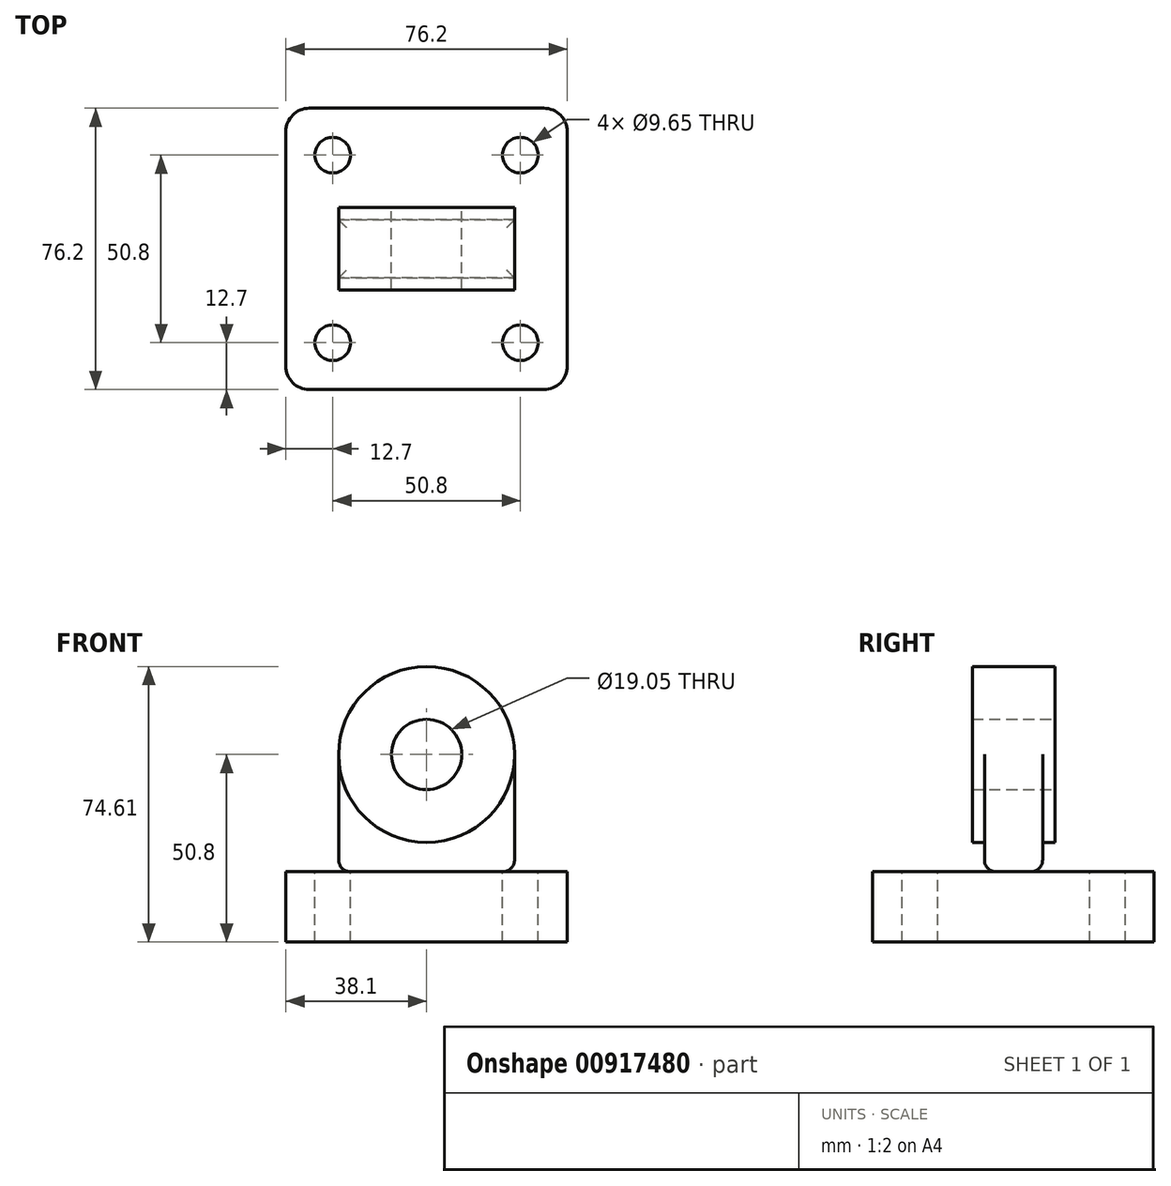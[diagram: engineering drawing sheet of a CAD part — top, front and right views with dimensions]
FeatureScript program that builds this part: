
annotation { "Feature Type Name" : "Feature", "Feature Type Description" : "" }
export const myFeature = defineFeature(function(context is Context, id is Id, definition is map)
    precondition{}
    {
        {
            var Q0;
            Q0=qCreatedBy(makeId("Top.planeOp"),FACE);
            var sketch = newSketch(context, id + "F0", { "sketchPlane" : qUnion([Q0])});
            skLineSegment(sketch, "E0.bottom", {"start": v(0, 0) * mm, "end": v(76.2, 0) * mm});
            skLineSegment(sketch, "E0.top", {"start": v(0, 76.2) * mm, "end": v(76.2, 76.2) * mm});
            skLineSegment(sketch, "E0.left", {"start": v(0, 0) * mm, "end": v(0, 76.2) * mm});
            skLineSegment(sketch, "E0.right", {"start": v(76.2, 0) * mm, "end": v(76.2, 76.2) * mm});
            skSolve(sketch);
        }
        {
            var Q0;
            Q0=makeQuery(id+"F0.imprint","IMPRINT",FACE,{"disambiguationData":[TD([[makeQuery(id+"F0.imprint","IMPRINT",EDGE,{"derivedFrom":sQuery(id+"F0.wireOp",EDGE,"E0.bottom")}),1.0]])]});
            extrude(context, id + "F1", {"entities" : qUnion([Q0]), "depth" : 19.05 * mm, "offsetDistance" : 25.4 * mm});
        }
        {
            var Q0;
            Q0=makeQuery(id+"F1.opExtrude","CAP_FACE",FACE,{"disambiguationData":[OSD([sQuery(id+"F0.wireOp",EDGE,"E0.bottom"),sQuery(id+"F0.wireOp",EDGE,"E0.top"),sQuery(id+"F0.wireOp",EDGE,"E0.left"),sQuery(id+"F0.wireOp",EDGE,"E0.right")])],"isStart":false});
            var sketch = newSketch(context, id + "F2", { "sketchPlane" : qUnion([Q0])});
            skPoint(sketch, "E1", {"position": v(12.7, 12.7) * mm});
            skPoint(sketch, "E2", {"position": v(63.5, 12.7) * mm});
            skPoint(sketch, "E3", {"position": v(12.7, 63.5) * mm});
            skPoint(sketch, "E4", {"position": v(63.5, 63.5) * mm});
            skSolve(sketch);
        }
        {
            var Q0;
            Q0=sQuery(id+"F2.wireOp",VERTEX,"E3");
            var Q1;
            Q1=sQuery(id+"F2.wireOp",VERTEX,"E4");
            var Q2;
            Q2=sQuery(id+"F2.wireOp",VERTEX,"E2");
            var Q3;
            Q3=sQuery(id+"F2.wireOp",VERTEX,"E1");
            var Q4;
            Q4=makeQuery(id+"F1.opExtrude","SWEPT_BODY",BODY,{"disambiguationData":[OSD([sQuery(id+"F0.wireOp",EDGE,"E0.bottom"),sQuery(id+"F0.wireOp",EDGE,"E0.top"),sQuery(id+"F0.wireOp",EDGE,"E0.left"),sQuery(id+"F0.wireOp",EDGE,"E0.right")])]});
            hole(context, id + "F3", {"style" : HoleStyle.SIMPLE, "endStyle" : HoleEndStyle.THROUGH, "holeDiameter" : 9.65 * mm, "majorDiameter" : 6.35 * mm, "isTappedThrough" : true, "tappedDepth" : 12.7 * mm, "tapClearance" : 3, "locations" : qUnion([Q0, Q1, Q2, Q3]), "scope" : qUnion([Q4])});
        }
        {
            var Q0;
            Q0=makeQuery(id+"F1.opExtrude","CAP_FACE",FACE,{"disambiguationData":[OSD([sQuery(id+"F0.wireOp",EDGE,"E0.bottom"),sQuery(id+"F0.wireOp",EDGE,"E0.top"),sQuery(id+"F0.wireOp",EDGE,"E0.left"),sQuery(id+"F0.wireOp",EDGE,"E0.right")])],"isStart":false});
            var sketch = newSketch(context, id + "F4", { "sketchPlane" : qUnion([Q0])});
            skLineSegment(sketch, "E5.bottom", {"start": v(61.91, 45.97) * mm, "end": v(14.29, 45.97) * mm});
            skLineSegment(sketch, "E5.top", {"start": v(61.91, 30.23) * mm, "end": v(14.29, 30.23) * mm});
            skLineSegment(sketch, "E5.left", {"start": v(61.91, 45.97) * mm, "end": v(61.91, 30.23) * mm});
            skLineSegment(sketch, "E5.right", {"start": v(14.29, 45.97) * mm, "end": v(14.29, 30.23) * mm});
            skPoint(sketch, "E5.middle", {"position": v(38.1, 38.1) * mm});
            skSolve(sketch);
        }
        {
            var Q0;
            Q0=makeQuery(id+"F4.imprint","IMPRINT",FACE,{"disambiguationData":[TD([[makeQuery(id+"F4.imprint","IMPRINT",EDGE,{"derivedFrom":sQuery(id+"F4.wireOp",EDGE,"E5.bottom")}),1.0]])]});
            extrude(context, id + "F5", {"entities" : qUnion([Q0]), "depth" : 55.56 * mm, "offsetDistance" : 25.4 * mm});
        }
        {
            var Q0;
            Q0=makeQuery(id+"F5.opExtrude","SWEPT_FACE",FACE,{"disambiguationData":[OSD([sQuery(id+"F4.wireOp",EDGE,"E5.bottom")])]});
            var sketch = newSketch(context, id + "F6", { "sketchPlane" : qUnion([Q0])});
            skCircle(sketch, "E6", {"center": v(-38.1, 50.8) * mm, "radius": 23.81 * mm});
            skCircle(sketch, "E7", {"center": v(-38.1, 50.8) * mm, "radius": 9.53 * mm});
            skSolve(sketch);
        }
        {
            var Q0;
            Q0=makeQuery(id+"F1.opExtrude","SWEPT_EDGE",EDGE,{"disambiguationData":[OSD([sQuery(id+"F0.wireOp",EDGE,"E0.top"),sQuery(id+"F0.wireOp",EDGE,"E0.left")])]});
            var Q1;
            Q1=makeQuery(id+"F1.opExtrude","SWEPT_EDGE",EDGE,{"disambiguationData":[OSD([sQuery(id+"F0.wireOp",EDGE,"E0.top"),sQuery(id+"F0.wireOp",EDGE,"E0.right")])]});
            var Q2;
            Q2=makeQuery(id+"F1.opExtrude","SWEPT_EDGE",EDGE,{"disambiguationData":[OSD([sQuery(id+"F0.wireOp",EDGE,"E0.bottom"),sQuery(id+"F0.wireOp",EDGE,"E0.left")])]});
            var Q3;
            Q3=makeQuery(id+"F1.opExtrude","SWEPT_EDGE",EDGE,{"disambiguationData":[OSD([sQuery(id+"F0.wireOp",EDGE,"E0.bottom"),sQuery(id+"F0.wireOp",EDGE,"E0.right")])]});
            fillet(context, id + "F7", {"entities" : qUnion([Q0, Q1, Q2, Q3]), "radius" : 6.35 * mm, "tangentPropagation" : true, "allowEdgeOverflow" : false});
        }
        {
            var Q0;
            {var subQ0=sQuery(id+"F6.wireOp",EDGE,"E6");var subQ1=sQuery(id+"F4.wireOp",EDGE,"E5.bottom");var subQ2=makeQuery(id+"F5.opExtrude","CAP_EDGE",EDGE,{"disambiguationData":[OSD([subQ1])],"isStart":false});var subQ3=makeQuery(id+"F6.imprint","INTERSECT",VERTEX,{"derivedFrom":[subQ2,subQ0]});Q0=makeQuery(id+"F6.imprint","IMPRINT",FACE,{"disambiguationData":[TD([[makeQuery(id+"F6.imprint","IMPRINT",EDGE,{"disambiguationData":[TD([[subQ3,-1.0]])],"derivedFrom":subQ0}),-1.0]])]});}
            var Q1;
            {var subQ0=sQuery(id+"F6.wireOp",EDGE,"E6");var subQ1=sQuery(id+"F4.wireOp",EDGE,"E5.bottom");var subQ2=makeQuery(id+"F5.opExtrude","CAP_EDGE",EDGE,{"disambiguationData":[OSD([subQ1])],"isStart":false});var subQ3=makeQuery(id+"F6.imprint","INTERSECT",VERTEX,{"derivedFrom":[subQ2,subQ0]});Q1=makeQuery(id+"F6.imprint","IMPRINT",FACE,{"disambiguationData":[TD([[makeQuery(id+"F6.imprint","IMPRINT",EDGE,{"disambiguationData":[TD([[subQ3,1.0]])],"derivedFrom":subQ0}),-1.0]])]});}
            extrude(context, id + "F8", {"entities" : qUnion([Q0, Q1]), "operationType" : NewBodyOperationType.REMOVE, "endBound" : BoundingType.THROUGH_ALL, "oppositeDirection" : true, "depth" : 25.4 * mm, "offsetDistance" : 25.4 * mm});
        }
        {
            var Q0;
            Q0=makeQuery(id+"F6.imprint","IMPRINT",FACE,{"disambiguationData":[TD([[makeQuery(id+"F6.imprint","IMPRINT",EDGE,{"derivedFrom":sQuery(id+"F6.wireOp",EDGE,"E7")}),1.0]])]});
            var Q1;
            Q1=sQuery(id+"F6.wireOp",EDGE,"E7");
            extrude(context, id + "F9", {"entities" : qUnion([Q0]), "operationType" : NewBodyOperationType.REMOVE, "surfaceEntities" : qUnion([Q1]), "endBound" : BoundingType.THROUGH_ALL, "oppositeDirection" : true, "depth" : 25.4 * mm, "offsetDistance" : 25.4 * mm});
        }
        {
            var Q0;
            Q0=makeQuery(id+"F6.imprint","IMPRINT",FACE,{"disambiguationData":[TD([[makeQuery(id+"F6.imprint","IMPRINT",EDGE,{"derivedFrom":sQuery(id+"F6.wireOp",EDGE,"E7")}),-1.0]])]});
            extrude(context, id + "F10", {"entities" : qUnion([Q0]), "operationType" : NewBodyOperationType.ADD, "depth" : 3.3 * mm, "offsetDistance" : 25.4 * mm, "hasSecondDirection" : true, "secondDirectionOppositeDirection" : true, "secondDirectionDepth" : 19.05 * mm});
        }
        {
            var Q0;
            Q0=makeQuery(id+"F5.opExtrude","CAP_EDGE",EDGE,{"disambiguationData":[OSD([sQuery(id+"F4.wireOp",EDGE,"E5.bottom")])],"isStart":true});
            var Q1;
            Q1=makeQuery(id+"F5.opExtrude","CAP_EDGE",EDGE,{"disambiguationData":[OSD([sQuery(id+"F4.wireOp",EDGE,"E5.right")])],"isStart":true});
            var Q2;
            Q2=makeQuery(id+"F5.opExtrude","CAP_EDGE",EDGE,{"disambiguationData":[OSD([sQuery(id+"F4.wireOp",EDGE,"E5.left")])],"isStart":true});
            var Q3;
            Q3=makeQuery(id+"F5.opExtrude","CAP_EDGE",EDGE,{"disambiguationData":[OSD([sQuery(id+"F4.wireOp",EDGE,"E5.top")])],"isStart":true});
            fillet(context, id + "F11", {"entities" : qUnion([Q0, Q1, Q2, Q3]), "radius" : 3.17 * mm, "tangentPropagation" : true, "allowEdgeOverflow" : false});
        }
    });
